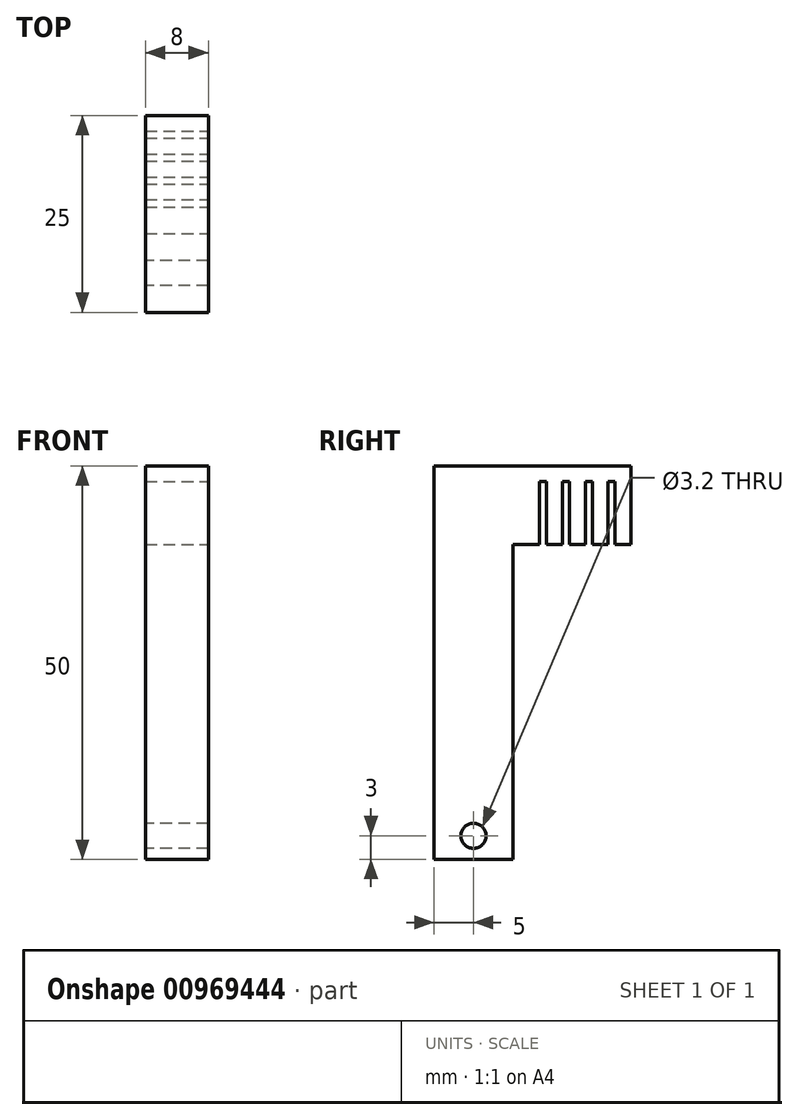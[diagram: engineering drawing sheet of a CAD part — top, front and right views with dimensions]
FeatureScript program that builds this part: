
annotation { "Feature Type Name" : "Feature", "Feature Type Description" : "" }
export const myFeature = defineFeature(function(context is Context, id is Id, definition is map)
    precondition{}
    {
        {
            var Q0;
            Q0=qCreatedBy(makeId("Top.planeOp"),FACE);
            var sketch = newSketch(context, id + "F0", { "sketchPlane" : qUnion([Q0])});
            skLineSegment(sketch, "E0.bottom", {"start": v(4, -12.5) * mm, "end": v(-4, -12.5) * mm});
            skLineSegment(sketch, "E0.top", {"start": v(4, 12.5) * mm, "end": v(-4, 12.5) * mm});
            skLineSegment(sketch, "E0.left", {"start": v(4, -12.5) * mm, "end": v(4, 12.5) * mm});
            skLineSegment(sketch, "E0.right", {"start": v(-4, -12.5) * mm, "end": v(-4, 12.5) * mm});
            skPoint(sketch, "E0.middle", {"position": v(0, 0) * mm});
            skSolve(sketch);
        }
        {
            var Q0;
            Q0=makeQuery(id+"F0.imprint","IMPRINT",FACE,{"disambiguationData":[TD([[makeQuery(id+"F0.imprint","IMPRINT",EDGE,{"derivedFrom":sQuery(id+"F0.wireOp",EDGE,"E0.bottom")}),-1.0]])]});
            extrude(context, id + "F1", {"entities" : qUnion([Q0]), "depth" : 10 * mm, "offsetDistance" : 25 * mm});
        }
        {
            var Q0;
            Q0=makeQuery(id+"F1.opExtrude","CAP_FACE",FACE,{"disambiguationData":[OSD([sQuery(id+"F0.wireOp",EDGE,"E0.bottom"),sQuery(id+"F0.wireOp",EDGE,"E0.top"),sQuery(id+"F0.wireOp",EDGE,"E0.left"),sQuery(id+"F0.wireOp",EDGE,"E0.right")])],"isStart":true});
            var sketch = newSketch(context, id + "F2", { "sketchPlane" : qUnion([Q0])});
            skLineSegment(sketch, "E1.bottom", {"start": v(-4, -10.5) * mm, "end": v(4, -10.5) * mm});
            skLineSegment(sketch, "E1.top", {"start": v(-4, -9.6) * mm, "end": v(4, -9.6) * mm});
            skLineSegment(sketch, "E1.left", {"start": v(-4, -10.5) * mm, "end": v(-4, -9.6) * mm});
            skLineSegment(sketch, "E1.right", {"start": v(4, -10.5) * mm, "end": v(4, -9.6) * mm});
            skLineSegment(sketch, "E2.bottom", {"start": v(-4, -7.6) * mm, "end": v(4, -7.6) * mm});
            skLineSegment(sketch, "E2.top", {"start": v(-4, -6.7) * mm, "end": v(4, -6.7) * mm});
            skLineSegment(sketch, "E2.left", {"start": v(-4, -7.6) * mm, "end": v(-4, -6.7) * mm});
            skLineSegment(sketch, "E2.right", {"start": v(4, -7.6) * mm, "end": v(4, -6.7) * mm});
            skLineSegment(sketch, "E3.bottom", {"start": v(-4, -4.7) * mm, "end": v(4, -4.7) * mm});
            skLineSegment(sketch, "E3.top", {"start": v(-4, -3.8) * mm, "end": v(4, -3.8) * mm});
            skLineSegment(sketch, "E3.left", {"start": v(-4, -4.7) * mm, "end": v(-4, -3.8) * mm});
            skLineSegment(sketch, "E3.right", {"start": v(4, -4.7) * mm, "end": v(4, -3.8) * mm});
            skLineSegment(sketch, "E4.bottom", {"start": v(-4, -0.9) * mm, "end": v(4, -0.9) * mm});
            skLineSegment(sketch, "E4.top", {"start": v(-4, -1.8) * mm, "end": v(4, -1.8) * mm});
            skLineSegment(sketch, "E4.left", {"start": v(-4, -0.9) * mm, "end": v(-4, -1.8) * mm});
            skLineSegment(sketch, "E4.right", {"start": v(4, -0.9) * mm, "end": v(4, -1.8) * mm});
            skSolve(sketch);
        }
        {
            var Q0;
            Q0=makeQuery(id+"F2.imprint","IMPRINT",FACE,{"disambiguationData":[TD([[makeQuery(id+"F2.imprint","IMPRINT",EDGE,{"derivedFrom":sQuery(id+"F2.wireOp",EDGE,"E1.bottom")}),1.0]])]});
            var Q1;
            Q1=makeQuery(id+"F2.imprint","IMPRINT",FACE,{"disambiguationData":[TD([[makeQuery(id+"F2.imprint","IMPRINT",EDGE,{"derivedFrom":sQuery(id+"F2.wireOp",EDGE,"E2.bottom")}),1.0]])]});
            var Q2;
            Q2=makeQuery(id+"F2.imprint","IMPRINT",FACE,{"disambiguationData":[TD([[makeQuery(id+"F2.imprint","IMPRINT",EDGE,{"derivedFrom":sQuery(id+"F2.wireOp",EDGE,"E3.bottom")}),1.0]])]});
            var Q3;
            Q3=makeQuery(id+"F2.imprint","IMPRINT",FACE,{"disambiguationData":[TD([[makeQuery(id+"F2.imprint","IMPRINT",EDGE,{"derivedFrom":sQuery(id+"F2.wireOp",EDGE,"E4.bottom")}),-1.0]])]});
            extrude(context, id + "F3", {"entities" : qUnion([Q0, Q1, Q2, Q3]), "operationType" : NewBodyOperationType.REMOVE, "oppositeDirection" : true, "depth" : 8 * mm, "offsetDistance" : 25 * mm});
        }
        {
            var Q0;
            {var subQ0=sQuery(id+"F0.wireOp",EDGE,"E0.bottom");var subQ1=sQuery(id+"F0.wireOp",EDGE,"E0.right");var subQ2=sQuery(id+"F0.wireOp",EDGE,"E0.left");Q0=makeQuery(id+"F3.boolean.opBoolean","SPLIT",FACE,{"disambiguationData":[TD([makeQuery(id+"F1.opExtrude","SWEPT_FACE",FACE,{"disambiguationData":[OSD([subQ0])]})])],"derivedFrom":makeQuery(id+"F1.opExtrude","CAP_FACE",FACE,{"disambiguationData":[OSD([subQ0,sQuery(id+"F0.wireOp",EDGE,"E0.top"),subQ2,subQ1])],"isStart":true})});}
            var sketch = newSketch(context, id + "F4", { "sketchPlane" : qUnion([Q0])});
            skLineSegment(sketch, "E5.bottom", {"start": v(-4, 12.5) * mm, "end": v(4, 12.5) * mm});
            skLineSegment(sketch, "E5.top", {"start": v(-4, 2.5) * mm, "end": v(4, 2.5) * mm});
            skLineSegment(sketch, "E5.left", {"start": v(-4, 12.5) * mm, "end": v(-4, 2.5) * mm});
            skLineSegment(sketch, "E5.right", {"start": v(4, 12.5) * mm, "end": v(4, 2.5) * mm});
            skSolve(sketch);
        }
        {
            var Q0;
            Q0=makeQuery(id+"F4.imprint","IMPRINT",FACE,{"disambiguationData":[TD([[makeQuery(id+"F4.imprint","IMPRINT",EDGE,{"derivedFrom":sQuery(id+"F4.wireOp",EDGE,"E5.bottom")}),1.0]])]});
            extrude(context, id + "F5", {"entities" : qUnion([Q0]), "operationType" : NewBodyOperationType.ADD, "depth" : 40 * mm, "offsetDistance" : 25 * mm});
        }
        {
            var Q0;
            Q0=makeQuery(id+"F5.boolean.opBoolean","MERGE",FACE,{"derivedFrom":[makeQuery(id+"F1.opExtrude","SWEPT_FACE",FACE,{"disambiguationData":[OSD([sQuery(id+"F0.wireOp",EDGE,"E0.right")])]}),makeQuery(id+"F5.opExtrude","SWEPT_FACE",FACE,{"disambiguationData":[OSD([sQuery(id+"F4.wireOp",EDGE,"E5.left")])]})]});
            var sketch = newSketch(context, id + "F6", { "sketchPlane" : qUnion([Q0])});
            skLineSegment(sketch, "E6", {"start": v(2.5, -37) * mm, "end": v(12.5, -37) * mm, "construction": true});
            skCircle(sketch, "E7", {"center": v(7.5, -37) * mm, "radius": 1.6 * mm});
            skSolve(sketch);
        }
        {
            var Q0;
            Q0=makeQuery(id+"F6.imprint","IMPRINT",FACE,{"disambiguationData":[TD([[makeQuery(id+"F6.imprint","IMPRINT",EDGE,{"derivedFrom":sQuery(id+"F6.wireOp",EDGE,"E7")}),1.0]])]});
            extrude(context, id + "F7", {"entities" : qUnion([Q0]), "operationType" : NewBodyOperationType.REMOVE, "endBound" : BoundingType.THROUGH_ALL, "oppositeDirection" : true, "depth" : 25 * mm, "offsetDistance" : 25 * mm});
        }
    });
